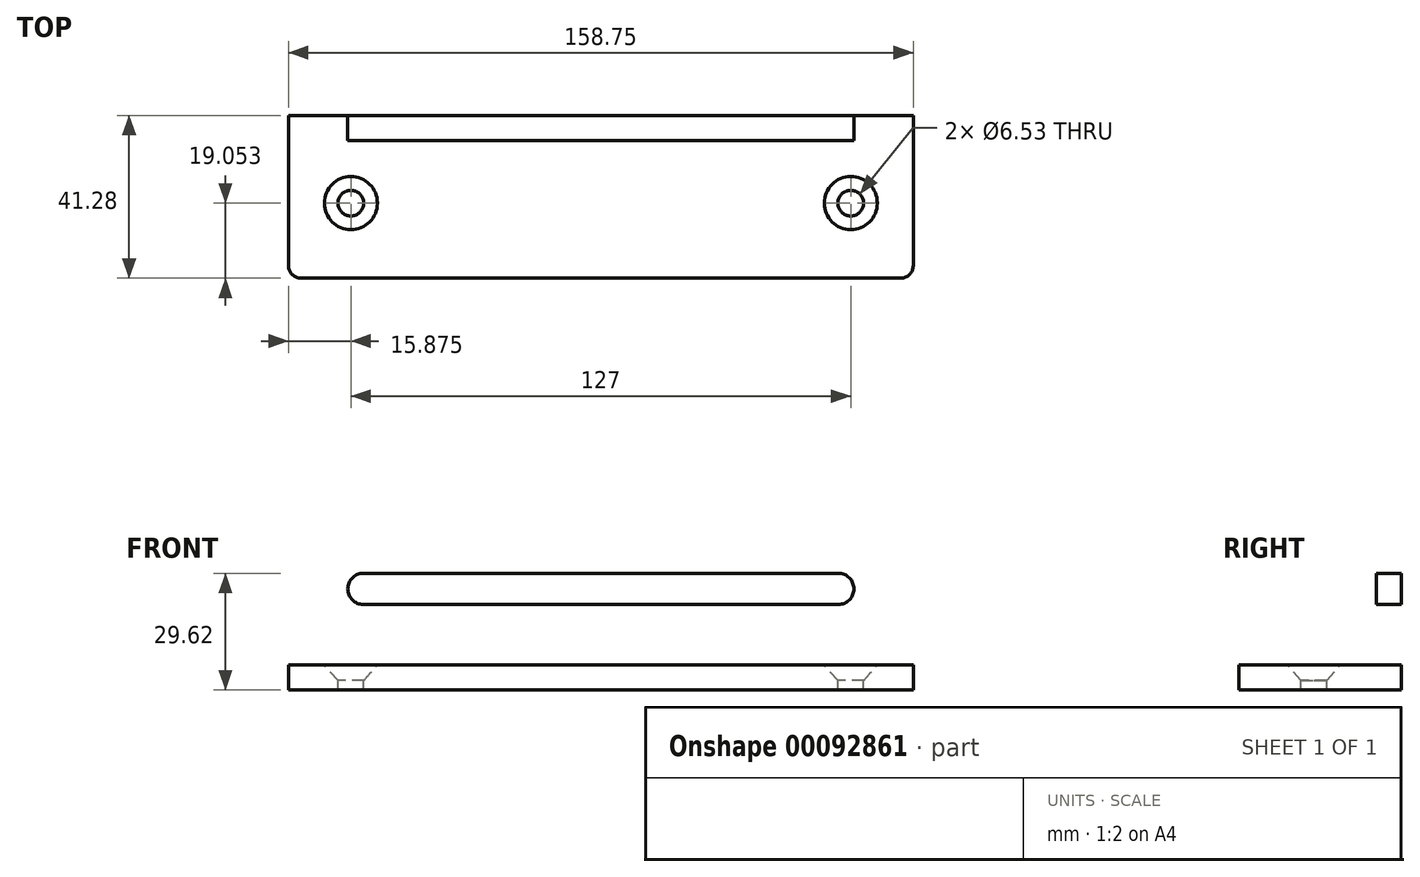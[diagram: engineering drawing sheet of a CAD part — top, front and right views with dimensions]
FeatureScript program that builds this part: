
annotation { "Feature Type Name" : "Feature", "Feature Type Description" : "" }
export const myFeature = defineFeature(function(context is Context, id is Id, definition is map)
    precondition{}
    {
        {
            var Q0;
            Q0=qCreatedBy(makeId("Right.planeOp"),FACE);
            var sketch = newSketch(context, id + "F0", { "sketchPlane" : qUnion([Q0])});
            skLineSegment(sketch, "E0.bottom", {"start": v(20.64, -20.64) * mm, "end": v(-20.64, -20.64) * mm, "construction": true});
            skLineSegment(sketch, "E0.top", {"start": v(20.64, 20.64) * mm, "end": v(-20.64, 20.64) * mm, "construction": true});
            skLineSegment(sketch, "E0.left", {"start": v(20.64, -20.64) * mm, "end": v(20.64, 20.64) * mm, "construction": true});
            skLineSegment(sketch, "E0.right", {"start": v(-20.64, -20.64) * mm, "end": v(-20.64, 20.64) * mm, "construction": true});
            skPoint(sketch, "E0.middle", {"position": v(0, 0) * mm});
            skLineSegment(sketch, "E1", {"start": v(14.29, 20.64) * mm, "end": v(14.29, -20.64) * mm, "construction": true});
            skLineSegment(sketch, "E2", {"start": v(-20.64, -14.29) * mm, "end": v(20.64, -14.29) * mm, "construction": true});
            skLineSegment(sketch, "E3", {"start": v(14.29, 20.64) * mm, "end": v(20.64, 20.64) * mm});
            skLineSegment(sketch, "E4", {"start": v(20.64, 20.64) * mm, "end": v(20.64, -20.64) * mm});
            skLineSegment(sketch, "E5", {"start": v(20.64, -20.64) * mm, "end": v(-20.64, -20.64) * mm});
            skLineSegment(sketch, "E6", {"start": v(-20.64, -20.64) * mm, "end": v(-20.64, -14.29) * mm});
            skLineSegment(sketch, "E7", {"start": v(-20.64, -14.29) * mm, "end": v(14.29, -14.29) * mm});
            skLineSegment(sketch, "E8", {"start": v(14.29, -14.29) * mm, "end": v(14.29, 20.64) * mm});
            skSolve(sketch);
        }
        {
            var Q0;
            Q0=makeQuery(id+"F0.imprint","IMPRINT",FACE,{"disambiguationData":[TD([[makeQuery(id+"F0.imprint","IMPRINT",EDGE,{"derivedFrom":sQuery(id+"F0.wireOp",EDGE,"E3")}),-1.0]])]});
            extrude(context, id + "F1", {"entities" : qUnion([Q0]), "depth" : 158.75 * mm});
        }
        {
            var Q0;
            Q0=makeQuery(id+"F1.opExtrude","SWEPT_FACE",FACE,{"disambiguationData":[OSD([sQuery(id+"F0.wireOp",EDGE,"E8")])]});
            var sketch = newSketch(context, id + "F2", { "sketchPlane" : qUnion([Q0])});
            skLineSegment(sketch, "E9", {"start": v(0, 5.02) * mm, "end": v(158.75, 5.02) * mm, "construction": true});
            skLineSegment(sketch, "E10", {"start": v(19.05, 20.64) * mm, "end": v(19.05, -20.84) * mm, "construction": true});
            skLineSegment(sketch, "E11", {"start": v(139.7, 20.64) * mm, "end": v(139.7, -21.16) * mm, "construction": true});
            skLineSegment(sketch, "E12", {"start": v(19.05, 5.02) * mm, "end": v(139.7, 5.02) * mm});
            skArc(sketch, "E13.0.startCap", {"start": v(19.05, 1.05) * mm, "mid": v(15.09, 5.02) * mm, "end": v(19.05, 8.98) * mm});
            skArc(sketch, "E13.0.endCap", {"start": v(139.7, 8.98) * mm, "mid": v(143.66, 5.02) * mm, "end": v(139.7, 1.05) * mm});
            skLineSegment(sketch, "E13.0.left", {"start": v(19.05, 8.98) * mm, "end": v(139.7, 8.98) * mm});
            skLineSegment(sketch, "E13.0.right", {"start": v(19.05, 1.05) * mm, "end": v(139.7, 1.05) * mm});
            skSolve(sketch);
        }
        {
            var Q0;
            Q0=makeQuery(id+"F2.imprint","IMPRINT",FACE,{"disambiguationData":[TD([[makeQuery(id+"F2.imprint","IMPRINT",EDGE,{"derivedFrom":sQuery(id+"F2.wireOp",EDGE,"E13.0.startCap")}),-1.0]])]});
            extrude(context, id + "F3", {"entities" : qUnion([Q0]), "operationType" : NewBodyOperationType.REMOVE, "endBound" : BoundingType.THROUGH_ALL, "oppositeDirection" : true, "depth" : 25.4 * mm});
        }
        {
            var Q0;
            Q0=makeQuery(id+"F1.opExtrude","SWEPT_FACE",FACE,{"disambiguationData":[OSD([sQuery(id+"F0.wireOp",EDGE,"E7")])]});
            var sketch = newSketch(context, id + "F4", { "sketchPlane" : qUnion([Q0])});
            skLineSegment(sketch, "E14", {"start": v(0, -1.59) * mm, "end": v(158.75, -1.59) * mm, "construction": true});
            skLineSegment(sketch, "E15", {"start": v(15.88, -20.64) * mm, "end": v(15.88, 14.29) * mm, "construction": true});
            skLineSegment(sketch, "E16", {"start": v(142.88, 14.29) * mm, "end": v(142.88, -20.64) * mm, "construction": true});
            skPoint(sketch, "E17", {"position": v(15.88, -1.59) * mm});
            skPoint(sketch, "E18", {"position": v(142.88, -1.59) * mm});
            skSolve(sketch);
        }
        {
            var Q0;
            Q0=sQuery(id+"F4.wireOp",VERTEX,"E17");
            var Q1;
            Q1=sQuery(id+"F4.wireOp",VERTEX,"E18");
            var Q2;
            Q2=makeQuery(id+"F1.opExtrude","SWEPT_BODY",BODY,{"disambiguationData":[OSD([sQuery(id+"F0.wireOp",EDGE,"E3"),sQuery(id+"F0.wireOp",EDGE,"E4"),sQuery(id+"F0.wireOp",EDGE,"E5"),sQuery(id+"F0.wireOp",EDGE,"E6"),sQuery(id+"F0.wireOp",EDGE,"E7"),sQuery(id+"F0.wireOp",EDGE,"E8")])]});
            hole(context, id + "F5", {"style" : HoleStyle.C_SINK, "endStyle" : HoleEndStyle.THROUGH, "standardTappedOrClearance" : lookupTablePath({ "standard" : "ANSI", "fit" : "Close", "size" : "1/4", "type" : "Clearance" }), "standardBlindInLast" : lookupTablePath({ "fit" : "Close", "standard" : "ANSI", "size" : "1/4", "type" : "Clearance" }), "holeDiameter" : 6.53 * mm, "cSinkDiameter" : 13.5 * mm, "cSinkAngle" : 82 * degree, "locations" : qUnion([Q0, Q1]), "scope" : qUnion([Q2]), "isTappedThrough" : true});
        }
        {
            var Q0;
            Q0=makeQuery(id+"F1.opExtrude","CAP_EDGE",EDGE,{"disambiguationData":[OSD([sQuery(id+"F0.wireOp",EDGE,"E3")])],"isStart":true});
            var Q1;
            Q1=makeQuery(id+"F1.opExtrude","CAP_EDGE",EDGE,{"disambiguationData":[OSD([sQuery(id+"F0.wireOp",EDGE,"E3")])],"isStart":false});
            var Q2;
            Q2=makeQuery(id+"F1.opExtrude","CAP_EDGE",EDGE,{"disambiguationData":[OSD([sQuery(id+"F0.wireOp",EDGE,"E6")])],"isStart":false});
            var Q3;
            Q3=makeQuery(id+"F1.opExtrude","CAP_EDGE",EDGE,{"disambiguationData":[OSD([sQuery(id+"F0.wireOp",EDGE,"E6")])],"isStart":true});
            fillet(context, id + "F6", {"entities" : qUnion([Q0, Q1, Q2, Q3]), "radius" : 3.17 * mm, "tangentPropagation" : true, "allowEdgeOverflow" : false});
        }
    });
